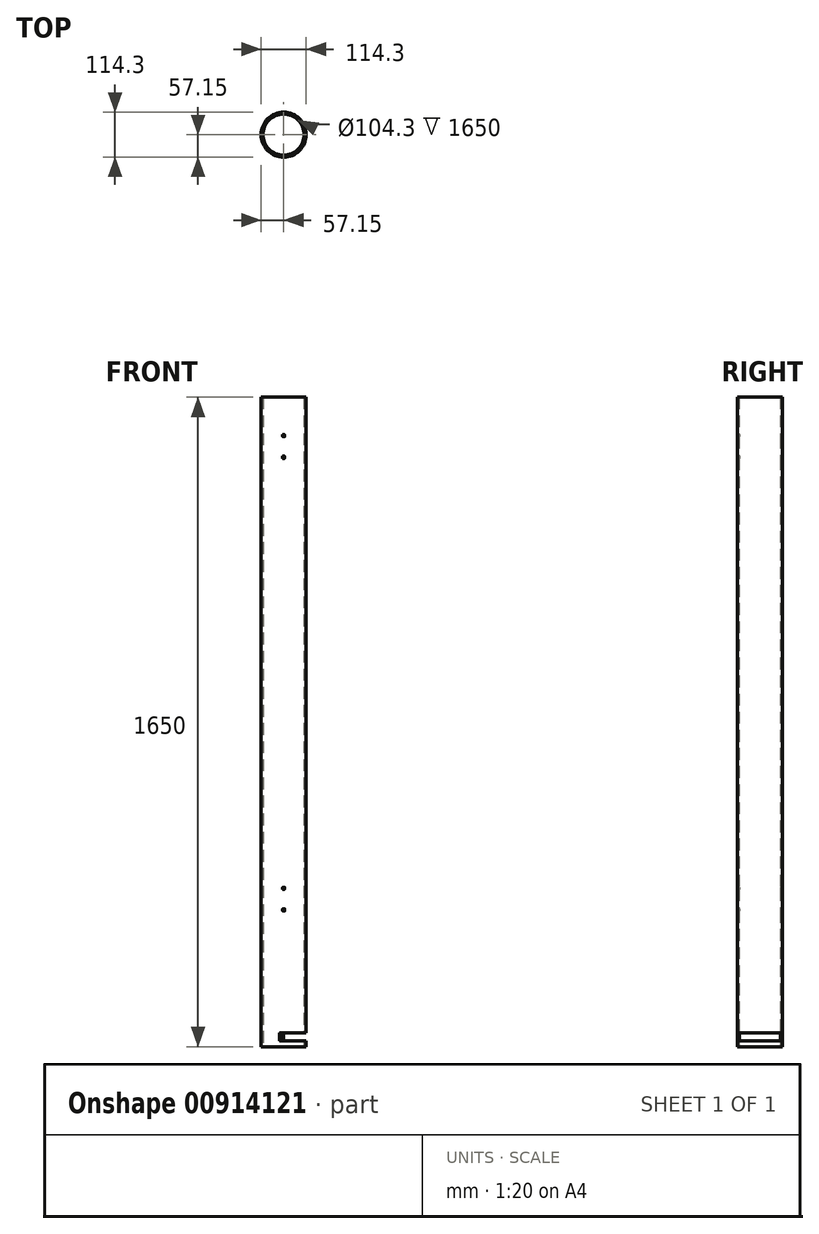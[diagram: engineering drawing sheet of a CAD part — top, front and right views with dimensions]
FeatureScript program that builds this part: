
annotation { "Feature Type Name" : "Feature", "Feature Type Description" : "" }
export const myFeature = defineFeature(function(context is Context, id is Id, definition is map)
    precondition{}
    {
        {
            var Q0;
            Q0=qCreatedBy(makeId("Top.planeOp"),FACE);
            var sketch = newSketch(context, id + "F0", { "sketchPlane" : qUnion([Q0])});
            skCircle(sketch, "E0", {"center": v(0, 0) * mm, "radius": 57.15 * mm});
            skCircle(sketch, "E1.0", {"center": v(0, 0) * mm, "radius": 52.15 * mm});
            skSolve(sketch);
        }
        {
            var Q0;
            Q0=makeQuery(id+"F0.imprint","IMPRINT",FACE,{"disambiguationData":[TD([[makeQuery(id+"F0.imprint","IMPRINT",EDGE,{"derivedFrom":sQuery(id+"F0.wireOp",EDGE,"E0")}),1.0]])]});
            extrude(context, id + "F1", {"entities" : qUnion([Q0]), "depth" : 1650 * mm, "offsetDistance" : 25 * mm});
        }
        {
            var Q0;
            Q0=qCreatedBy(makeId("Right.planeOp"),FACE);
            var sketch = newSketch(context, id + "F2", { "sketchPlane" : qUnion([Q0])});
            skLineSegment(sketch, "E2.bottom", {"start": v(52.15, 15) * mm, "end": v(57.15, 15) * mm});
            skLineSegment(sketch, "E2.top", {"start": v(52.15, 35) * mm, "end": v(57.15, 35) * mm});
            skLineSegment(sketch, "E2.left", {"start": v(52.15, 15) * mm, "end": v(52.15, 35) * mm});
            skLineSegment(sketch, "E2.right", {"start": v(57.15, 15) * mm, "end": v(57.15, 35) * mm});
            skLineSegment(sketch, "E3", {"start": v(-57.15, 0) * mm, "end": v(-57.15, 1550) * mm, "construction": true});
            skLineSegment(sketch, "E4", {"start": v(57.15, 1550) * mm, "end": v(57.15, 0) * mm, "construction": true});
            skPoint(sketch, "E5.visualSharp", {"position": v(52.15, 35) * mm});
            skLineSegment(sketch, "E6", {"start": v(-52.15, 0) * mm, "end": v(-52.15, 1650) * mm, "construction": true});
            skLineSegment(sketch, "E7", {"start": v(52.15, 1650) * mm, "end": v(52.15, 0) * mm, "construction": true});
            skSolve(sketch);
        }
        {
            var Q0;
            Q0 = qSketchRegion(id + "F2", true);
            var Q1;
            Q1=makeQuery(id+"F1.opExtrude","SWEPT_FACE",FACE,{"disambiguationData":[OSD([sQuery(id+"F0.wireOp",EDGE,"E0")])]});
            revolve(context, id + "F3", {"operationType" : NewBodyOperationType.REMOVE, "surfaceOperationType" : NewSurfaceOperationType.NEW, "entities" : qUnion([Q0]), "axis" : qUnion([Q1]), "revolveType" : RevolveType.ONE_DIRECTION, "angle" : 190 * degree});
        }
        {
            var Q0;
            Q0=makeQuery(id+"F3.boolean.opBoolean","COPY",EDGE,{"derivedFrom":makeQuery(id+"F3.opRevolve","CAP_EDGE",EDGE,{"disambiguationData":[OSD([sQuery(id+"F2.wireOp",EDGE,"E2.top")])],"isStart":false})});
            var Q1;
            Q1=makeQuery(id+"F3.boolean.opBoolean","COPY",EDGE,{"derivedFrom":makeQuery(id+"F3.opRevolve","CAP_EDGE",EDGE,{"disambiguationData":[OSD([sQuery(id+"F2.wireOp",EDGE,"E2.bottom")])],"isStart":false})});
            var Q2;
            Q2=makeQuery(id+"F3.boolean.opBoolean","COPY",EDGE,{"derivedFrom":makeQuery(id+"F3.opRevolve","CAP_EDGE",EDGE,{"disambiguationData":[OSD([sQuery(id+"F2.wireOp",EDGE,"E2.top")])],"isStart":true})});
            var Q3;
            Q3=makeQuery(id+"F3.boolean.opBoolean","COPY",EDGE,{"derivedFrom":makeQuery(id+"F3.opRevolve","CAP_EDGE",EDGE,{"disambiguationData":[OSD([sQuery(id+"F2.wireOp",EDGE,"E2.bottom")])],"isStart":true})});
            fillet(context, id + "F4", {"entities" : qUnion([Q0, Q1, Q2, Q3]), "radius" : 0.2 * mm, "tangentPropagation" : true, "allowEdgeOverflow" : false});
        }
        {
            var Q0;
            Q0=qCreatedBy(makeId("Front.planeOp"),FACE);
            var sketch = newSketch(context, id + "F5", { "sketchPlane" : qUnion([Q0])});
            skPoint(sketch, "E8", {"position": v(2.75, 1525) * mm});
            skPoint(sketch, "E9", {"position": v(2.75, 375) * mm});
            skLineSegment(sketch, "E10.bottom", {"start": v(-2.55, 350.25) * mm, "end": v(2.55, 350.25) * mm});
            skLineSegment(sketch, "E10.top", {"start": v(-2.55, 344.75) * mm, "end": v(2.55, 344.75) * mm});
            skLineSegment(sketch, "E10.left", {"start": v(-2.75, 350.05) * mm, "end": v(-2.75, 344.95) * mm});
            skLineSegment(sketch, "E10.right", {"start": v(2.75, 350.05) * mm, "end": v(2.75, 344.95) * mm});
            skLineSegment(sketch, "E11.bottom", {"start": v(-2.55, 405.25) * mm, "end": v(2.55, 405.25) * mm});
            skLineSegment(sketch, "E11.top", {"start": v(-2.55, 399.75) * mm, "end": v(2.55, 399.75) * mm});
            skLineSegment(sketch, "E11.left", {"start": v(-2.75, 405.05) * mm, "end": v(-2.75, 399.95) * mm});
            skLineSegment(sketch, "E11.right", {"start": v(2.75, 405.05) * mm, "end": v(2.75, 399.95) * mm});
            skPoint(sketch, "E12", {"position": v(2.75, 347.5) * mm});
            skPoint(sketch, "E13", {"position": v(2.75, 402.5) * mm});
            skLineSegment(sketch, "E14", {"start": v(2.75, 375) * mm, "end": v(-2.75, 375) * mm, "construction": true});
            skPoint(sketch, "E15.0.visualSharp", {"position": v(2.75, 399.75) * mm});
            skArc(sketch, "E15.0.filletArc", {"start": v(2.55, 399.75) * mm, "mid": v(2.7, 399.8) * mm, "end": v(2.75, 399.95) * mm});
            skPoint(sketch, "E16.0.visualSharp", {"position": v(2.75, 405.25) * mm});
            skArc(sketch, "E16.0.filletArc", {"start": v(2.75, 405.05) * mm, "mid": v(2.7, 405.2) * mm, "end": v(2.55, 405.25) * mm});
            skPoint(sketch, "E17.0.visualSharp", {"position": v(-2.75, 405.25) * mm});
            skArc(sketch, "E17.0.filletArc", {"start": v(-2.55, 405.25) * mm, "mid": v(-2.7, 405.2) * mm, "end": v(-2.75, 405.05) * mm});
            skPoint(sketch, "E18.0.visualSharp", {"position": v(-2.75, 399.75) * mm});
            skArc(sketch, "E18.0.filletArc", {"start": v(-2.75, 399.95) * mm, "mid": v(-2.7, 399.8) * mm, "end": v(-2.55, 399.75) * mm});
            skPoint(sketch, "E19.0.visualSharp", {"position": v(2.75, 350.25) * mm});
            skArc(sketch, "E19.0.filletArc", {"start": v(2.75, 350.05) * mm, "mid": v(2.7, 350.2) * mm, "end": v(2.55, 350.25) * mm});
            skPoint(sketch, "E20.0.visualSharp", {"position": v(-2.75, 350.25) * mm});
            skArc(sketch, "E20.0.filletArc", {"start": v(-2.55, 350.25) * mm, "mid": v(-2.7, 350.2) * mm, "end": v(-2.75, 350.05) * mm});
            skPoint(sketch, "E21.0.visualSharp", {"position": v(-2.75, 344.75) * mm});
            skArc(sketch, "E21.0.filletArc", {"start": v(-2.75, 344.95) * mm, "mid": v(-2.7, 344.8) * mm, "end": v(-2.55, 344.75) * mm});
            skPoint(sketch, "E22.0.visualSharp", {"position": v(2.75, 344.75) * mm});
            skArc(sketch, "E22.0.filletArc", {"start": v(2.55, 344.75) * mm, "mid": v(2.7, 344.8) * mm, "end": v(2.75, 344.95) * mm});
            skLineSegment(sketch, "E23", {"start": v(2.75, 1525) * mm, "end": v(-2.75, 1525) * mm, "construction": true});
            skLineSegment(sketch, "E24.bottom", {"start": v(-2.55, 1555.25) * mm, "end": v(2.55, 1555.25) * mm});
            skLineSegment(sketch, "E24.top", {"start": v(-2.55, 1549.75) * mm, "end": v(2.55, 1549.75) * mm});
            skLineSegment(sketch, "E24.left", {"start": v(-2.75, 1555.05) * mm, "end": v(-2.75, 1549.95) * mm});
            skLineSegment(sketch, "E24.right", {"start": v(2.75, 1555.05) * mm, "end": v(2.75, 1549.95) * mm});
            skLineSegment(sketch, "E25.bottom", {"start": v(-2.55, 1500.25) * mm, "end": v(2.55, 1500.25) * mm});
            skLineSegment(sketch, "E25.top", {"start": v(-2.55, 1494.75) * mm, "end": v(2.55, 1494.75) * mm});
            skLineSegment(sketch, "E25.left", {"start": v(-2.75, 1500.05) * mm, "end": v(-2.75, 1494.95) * mm});
            skLineSegment(sketch, "E25.right", {"start": v(2.75, 1500.05) * mm, "end": v(2.75, 1494.95) * mm});
            skPoint(sketch, "E26", {"position": v(2.75, 1552.5) * mm});
            skPoint(sketch, "E27", {"position": v(2.75, 1497.5) * mm});
            skPoint(sketch, "E28.0.visualSharp", {"position": v(2.75, 1500.25) * mm});
            skArc(sketch, "E28.0.filletArc", {"start": v(2.75, 1500.05) * mm, "mid": v(2.7, 1500.2) * mm, "end": v(2.55, 1500.25) * mm});
            skPoint(sketch, "E29.0.visualSharp", {"position": v(-2.75, 1500.25) * mm});
            skArc(sketch, "E29.0.filletArc", {"start": v(-2.55, 1500.25) * mm, "mid": v(-2.7, 1500.2) * mm, "end": v(-2.75, 1500.05) * mm});
            skPoint(sketch, "E30.0.visualSharp", {"position": v(-2.75, 1494.75) * mm});
            skArc(sketch, "E30.0.filletArc", {"start": v(-2.75, 1494.95) * mm, "mid": v(-2.7, 1494.8) * mm, "end": v(-2.55, 1494.75) * mm});
            skPoint(sketch, "E31.0.visualSharp", {"position": v(2.75, 1494.75) * mm});
            skArc(sketch, "E31.0.filletArc", {"start": v(2.55, 1494.75) * mm, "mid": v(2.7, 1494.8) * mm, "end": v(2.75, 1494.95) * mm});
            skPoint(sketch, "E32.0.visualSharp", {"position": v(2.75, 1549.75) * mm});
            skArc(sketch, "E32.0.filletArc", {"start": v(2.55, 1549.75) * mm, "mid": v(2.7, 1549.8) * mm, "end": v(2.75, 1549.95) * mm});
            skPoint(sketch, "E33.0.visualSharp", {"position": v(-2.75, 1549.75) * mm});
            skArc(sketch, "E33.0.filletArc", {"start": v(-2.75, 1549.95) * mm, "mid": v(-2.7, 1549.8) * mm, "end": v(-2.55, 1549.75) * mm});
            skArc(sketch, "E33.1.filletArc", {"start": v(-2.75, 1549.95) * mm, "mid": v(-2.7, 1549.8) * mm, "end": v(-2.55, 1549.75) * mm});
            skPoint(sketch, "E34.0.visualSharp", {"position": v(-2.75, 1555.25) * mm});
            skArc(sketch, "E34.0.filletArc", {"start": v(-2.55, 1555.25) * mm, "mid": v(-2.7, 1555.2) * mm, "end": v(-2.75, 1555.05) * mm});
            skPoint(sketch, "E35.0.visualSharp", {"position": v(2.75, 1555.25) * mm});
            skArc(sketch, "E35.0.filletArc", {"start": v(2.75, 1555.05) * mm, "mid": v(2.7, 1555.2) * mm, "end": v(2.55, 1555.25) * mm});
            skSolve(sketch);
        }
        {
            var Q0;
            Q0 = qSketchRegion(id + "F5", true);
            extrude(context, id + "F6", {"entities" : qUnion([Q0]), "operationType" : NewBodyOperationType.REMOVE, "endBound" : BoundingType.THROUGH_ALL, "oppositeDirection" : true, "depth" : 25 * mm, "offsetDistance" : 25 * mm, "hasSecondDirection" : true, "secondDirectionBound" : BoundingType.THROUGH_ALL, "secondDirectionOppositeDirection" : false, "secondDirectionDepth" : 25 * mm});
        }
        {
            var Q0;
            Q0=qCreatedBy(makeId("Top.planeOp"),FACE);
            cPlane(context, id + "F7", {"entities" : qUnion([Q0]), "cplaneType" : CPlaneType.OFFSET, "offset" : 305 * mm, "width" : 150 * mm, "height" : 150 * mm});
        }
        {
            var Q0;
            Q0=qCreatedBy(makeId("Top.planeOp"),FACE);
            cPlane(context, id + "F8", {"entities" : qUnion([Q0]), "cplaneType" : CPlaneType.OFFSET, "offset" : 300 * mm, "width" : 150 * mm, "height" : 150 * mm});
        }
        {
            var Q0;
            Q0=qCreatedBy(makeId("Top.planeOp"),FACE);
            cPlane(context, id + "F9", {"entities" : qUnion([Q0]), "cplaneType" : CPlaneType.OFFSET, "offset" : 60 * mm, "width" : 150 * mm, "height" : 150 * mm});
        }
    });
